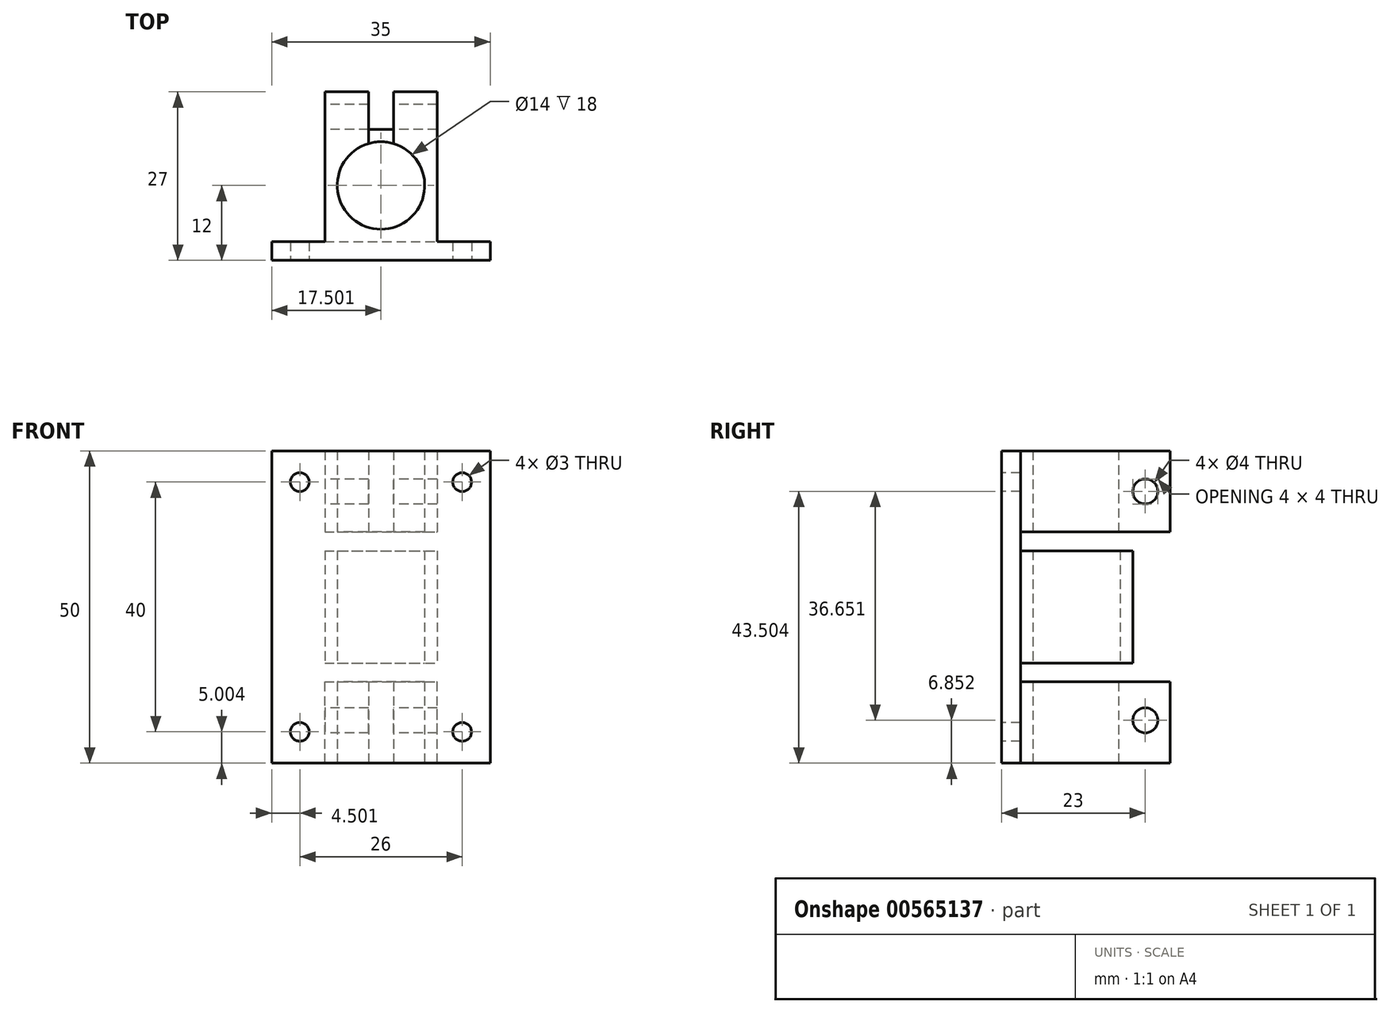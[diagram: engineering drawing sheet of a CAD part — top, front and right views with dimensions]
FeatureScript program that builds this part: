
annotation { "Feature Type Name" : "Feature", "Feature Type Description" : "" }
export const myFeature = defineFeature(function(context is Context, id is Id, definition is map)
    precondition{}
    {
        {
            var Q0;
            Q0=qCreatedBy(makeId("Front.planeOp"),FACE);
            var sketch = newSketch(context, id + "F0", { "sketchPlane" : qUnion([Q0])});
            skLineSegment(sketch, "E0.bottom", {"start": v(20, 24.93) * mm, "end": v(-15, 24.93) * mm});
            skLineSegment(sketch, "E0.top", {"start": v(20, -25.07) * mm, "end": v(-15, -25.07) * mm});
            skLineSegment(sketch, "E0.left", {"start": v(20, 24.93) * mm, "end": v(20, -25.07) * mm});
            skLineSegment(sketch, "E0.right", {"start": v(-15, 24.93) * mm, "end": v(-15, -25.07) * mm});
            skPoint(sketch, "E0.middle", {"position": v(2.5, -0.07) * mm});
            skSolve(sketch);
        }
        {
            var Q0;
            Q0=makeQuery(id+"F0.imprint","IMPRINT",FACE,{"disambiguationData":[TD([[makeQuery(id+"F0.imprint","IMPRINT",EDGE,{"derivedFrom":sQuery(id+"F0.wireOp",EDGE,"E0.bottom")}),1.0]])]});
            extrude(context, id + "F1", {"entities" : qUnion([Q0]), "oppositeDirection" : true, "depth" : 3 * mm, "offsetDistance" : 25 * mm});
        }
        {
            var Q0;
            Q0=makeQuery(id+"F1.opExtrude","CAP_FACE",FACE,{"disambiguationData":[OSD([sQuery(id+"F0.wireOp",EDGE,"E0.bottom"),sQuery(id+"F0.wireOp",EDGE,"E0.top"),sQuery(id+"F0.wireOp",EDGE,"E0.left"),sQuery(id+"F0.wireOp",EDGE,"E0.right")])],"isStart":false});
            var sketch = newSketch(context, id + "F2", { "sketchPlane" : qUnion([Q0])});
            skLineSegment(sketch, "E1.bottom", {"start": v(6.5, 24.93) * mm, "end": v(-11.5, 24.93) * mm});
            skLineSegment(sketch, "E1.top", {"start": v(6.5, 11.93) * mm, "end": v(-11.5, 11.93) * mm});
            skLineSegment(sketch, "E1.left", {"start": v(6.5, 24.93) * mm, "end": v(6.5, 11.93) * mm});
            skLineSegment(sketch, "E1.right", {"start": v(-11.5, 24.93) * mm, "end": v(-11.5, 11.93) * mm});
            skPoint(sketch, "E1.middle", {"position": v(-2.5, 18.43) * mm});
            skPoint(sketch, "E1.middle.positionSnap0", {"position": v(-2.5, 24.93) * mm});
            skPoint(sketch, "E1.centerSnap0", {"position": v(-2.5, 24.93) * mm});
            skLineSegment(sketch, "E2.bottom", {"start": v(6.5, 8.93) * mm, "end": v(-11.5, 8.93) * mm});
            skLineSegment(sketch, "E2.top", {"start": v(6.5, -9.07) * mm, "end": v(-11.5, -9.07) * mm});
            skLineSegment(sketch, "E2.left", {"start": v(6.5, 8.93) * mm, "end": v(6.5, -9.07) * mm});
            skLineSegment(sketch, "E2.right", {"start": v(-11.5, 8.93) * mm, "end": v(-11.5, -9.07) * mm});
            skPoint(sketch, "E2.middle", {"position": v(-2.5, -0.07) * mm});
            skLineSegment(sketch, "E3.bottom", {"start": v(6.5, -25.07) * mm, "end": v(-11.5, -25.07) * mm});
            skLineSegment(sketch, "E3.top", {"start": v(6.5, -12.07) * mm, "end": v(-11.5, -12.07) * mm});
            skLineSegment(sketch, "E3.left", {"start": v(6.5, -25.07) * mm, "end": v(6.5, -12.07) * mm});
            skLineSegment(sketch, "E3.right", {"start": v(-11.5, -25.07) * mm, "end": v(-11.5, -12.07) * mm});
            skPoint(sketch, "E3.middle", {"position": v(-2.5, -18.57) * mm});
            skSolve(sketch);
        }
        {
            var Q0;
            Q0=makeQuery(id+"F2.imprint","IMPRINT",FACE,{"disambiguationData":[TD([[makeQuery(id+"F2.imprint","IMPRINT",EDGE,{"derivedFrom":sQuery(id+"F2.wireOp",EDGE,"E1.bottom")}),-1.0]])]});
            var Q1;
            Q1=makeQuery(id+"F2.imprint","IMPRINT",FACE,{"disambiguationData":[TD([[makeQuery(id+"F2.imprint","IMPRINT",EDGE,{"derivedFrom":sQuery(id+"F2.wireOp",EDGE,"E2.bottom")}),1.0]])]});
            var Q2;
            Q2=makeQuery(id+"F2.imprint","IMPRINT",FACE,{"disambiguationData":[TD([[makeQuery(id+"F2.imprint","IMPRINT",EDGE,{"derivedFrom":sQuery(id+"F2.wireOp",EDGE,"E3.bottom")}),1.0]])]});
            extrude(context, id + "F3", {"entities" : qUnion([Q0, Q1, Q2]), "operationType" : NewBodyOperationType.ADD, "depth" : 24 * mm, "offsetDistance" : 25 * mm});
        }
        {
            var Q0;
            Q0=makeQuery(id+"F3.boolean.opBoolean","MERGE",FACE,{"derivedFrom":[makeQuery(id+"F1.opExtrude","SWEPT_FACE",FACE,{"disambiguationData":[OSD([sQuery(id+"F0.wireOp",EDGE,"E0.top")])]}),makeQuery(id+"F3.opExtrude","SWEPT_FACE",FACE,{"disambiguationData":[OSD([sQuery(id+"F2.wireOp",EDGE,"E3.bottom")])]})]});
            var sketch = newSketch(context, id + "F4", { "sketchPlane" : qUnion([Q0])});
            skCircle(sketch, "E4", {"center": v(2.5, -12) * mm, "radius": 7 * mm});
            skSolve(sketch);
        }
        {
            var Q0;
            Q0 = qSketchRegion(id + "F4", true);
            extrude(context, id + "F5", {"entities" : qUnion([Q0]), "operationType" : NewBodyOperationType.REMOVE, "oppositeDirection" : true, "depth" : 50 * mm, "offsetDistance" : 25 * mm});
        }
        {
            var Q0;
            Q0=makeQuery(id+"F3.opExtrude","SWEPT_FACE",FACE,{"disambiguationData":[OSD([sQuery(id+"F2.wireOp",EDGE,"E1.left")])]});
            var sketch = newSketch(context, id + "F6", { "sketchPlane" : qUnion([Q0])});
            skCircle(sketch, "E5", {"center": v(-23, 18.43) * mm, "radius": 2 * mm});
            skPoint(sketch, "E5.centerSnap0", {"position": v(-27, 18.43) * mm});
            skCircle(sketch, "E6", {"center": v(-23, -18.22) * mm, "radius": 2 * mm});
            skSolve(sketch);
        }
        {
            var Q0;
            Q0=makeQuery(id+"F6.imprint","IMPRINT",FACE,{"disambiguationData":[TD([[makeQuery(id+"F6.imprint","IMPRINT",EDGE,{"derivedFrom":sQuery(id+"F6.wireOp",EDGE,"E5")}),1.0]])]});
            var Q1;
            Q1=makeQuery(id+"F6.imprint","IMPRINT",FACE,{"disambiguationData":[TD([[makeQuery(id+"F6.imprint","IMPRINT",EDGE,{"derivedFrom":sQuery(id+"F6.wireOp",EDGE,"E6")}),1.0]])]});
            extrude(context, id + "F7", {"entities" : qUnion([Q0, Q1]), "operationType" : NewBodyOperationType.REMOVE, "oppositeDirection" : true, "depth" : 25 * mm, "offsetDistance" : 25 * mm});
        }
        {
            var Q0;
            Q0=makeQuery(id+"F3.opExtrude","CAP_FACE",FACE,{"disambiguationData":[OSD([sQuery(id+"F2.wireOp",EDGE,"E1.bottom"),sQuery(id+"F2.wireOp",EDGE,"E1.top"),sQuery(id+"F2.wireOp",EDGE,"E1.left"),sQuery(id+"F2.wireOp",EDGE,"E1.right")])],"isStart":false});
            var sketch = newSketch(context, id + "F8", { "sketchPlane" : qUnion([Q0])});
            skLineSegment(sketch, "E7", {"start": v(-2.5, 24.93) * mm, "end": v(-2.5, 11.93) * mm, "construction": true});
            skLineSegment(sketch, "E8", {"start": v(-2.5, 11.93) * mm, "end": v(-11.5, 18.43) * mm, "construction": true});
            skLineSegment(sketch, "E9", {"start": v(-11.5, 18.43) * mm, "end": v(6.5, 18.43) * mm, "construction": true});
            skLineSegment(sketch, "E10.bottom", {"start": v(-0.5, 24.93) * mm, "end": v(-4.5, 24.93) * mm});
            skLineSegment(sketch, "E10.top", {"start": v(-0.5, 11.93) * mm, "end": v(-4.5, 11.93) * mm});
            skLineSegment(sketch, "E10.left", {"start": v(-0.5, 24.93) * mm, "end": v(-0.5, 11.93) * mm});
            skLineSegment(sketch, "E10.right", {"start": v(-4.5, 24.93) * mm, "end": v(-4.5, 11.93) * mm});
            skPoint(sketch, "E10.middle", {"position": v(-2.5, 18.43) * mm});
            skSolve(sketch);
        }
        {
            var Q0;
            Q0=makeQuery(id+"F8.imprint","IMPRINT",FACE,{"disambiguationData":[TD([[makeQuery(id+"F8.imprint","IMPRINT",EDGE,{"derivedFrom":sQuery(id+"F8.wireOp",EDGE,"E10.bottom")}),-1.0]])]});
            extrude(context, id + "F9", {"entities" : qUnion([Q0]), "operationType" : NewBodyOperationType.REMOVE, "oppositeDirection" : true, "depth" : 10 * mm, "offsetDistance" : 25 * mm});
        }
        {
            var Q0;
            Q0=makeQuery(id+"F3.opExtrude","CAP_FACE",FACE,{"disambiguationData":[OSD([sQuery(id+"F2.wireOp",EDGE,"E3.bottom"),sQuery(id+"F2.wireOp",EDGE,"E3.top"),sQuery(id+"F2.wireOp",EDGE,"E3.left"),sQuery(id+"F2.wireOp",EDGE,"E3.right")])],"isStart":false});
            var sketch = newSketch(context, id + "F10", { "sketchPlane" : qUnion([Q0])});
            skLineSegment(sketch, "E11", {"start": v(-2.5, -12.07) * mm, "end": v(-2.5, -25.07) * mm, "construction": true});
            skLineSegment(sketch, "E12", {"start": v(-2.5, -25.07) * mm, "end": v(-11.5, -18.57) * mm, "construction": true});
            skLineSegment(sketch, "E13", {"start": v(-11.5, -18.57) * mm, "end": v(6.5, -18.57) * mm, "construction": true});
            skLineSegment(sketch, "E14.bottom", {"start": v(-0.5, -12.07) * mm, "end": v(-4.5, -12.07) * mm});
            skLineSegment(sketch, "E14.top", {"start": v(-0.5, -25.07) * mm, "end": v(-4.5, -25.07) * mm});
            skLineSegment(sketch, "E14.left", {"start": v(-0.5, -12.07) * mm, "end": v(-0.5, -25.07) * mm});
            skLineSegment(sketch, "E14.right", {"start": v(-4.5, -12.07) * mm, "end": v(-4.5, -25.07) * mm});
            skPoint(sketch, "E14.middle", {"position": v(-2.5, -18.57) * mm});
            skSolve(sketch);
        }
        {
            var Q0;
            Q0=makeQuery(id+"F10.imprint","IMPRINT",FACE,{"disambiguationData":[TD([[makeQuery(id+"F10.imprint","IMPRINT",EDGE,{"derivedFrom":sQuery(id+"F10.wireOp",EDGE,"E14.bottom")}),1.0]])]});
            extrude(context, id + "F11", {"entities" : qUnion([Q0]), "operationType" : NewBodyOperationType.REMOVE, "oppositeDirection" : true, "depth" : 10 * mm, "offsetDistance" : 25 * mm});
        }
        {
            var Q0;
            Q0=makeQuery(id+"F1.opExtrude","CAP_FACE",FACE,{"disambiguationData":[OSD([sQuery(id+"F0.wireOp",EDGE,"E0.bottom"),sQuery(id+"F0.wireOp",EDGE,"E0.top"),sQuery(id+"F0.wireOp",EDGE,"E0.left"),sQuery(id+"F0.wireOp",EDGE,"E0.right")])],"isStart":true});
            var sketch = newSketch(context, id + "F12", { "sketchPlane" : qUnion([Q0])});
            skCircle(sketch, "E15", {"center": v(-10.5, 19.93) * mm, "radius": 1.5 * mm});
            skCircle(sketch, "E16", {"center": v(15.5, 19.93) * mm, "radius": 1.5 * mm});
            skCircle(sketch, "E17", {"center": v(-10.5, -20.07) * mm, "radius": 1.5 * mm});
            skCircle(sketch, "E18", {"center": v(15.5, -20.07) * mm, "radius": 1.5 * mm});
            skSolve(sketch);
        }
        {
            var Q0;
            Q0=makeQuery(id+"F12.imprint","IMPRINT",FACE,{"disambiguationData":[TD([[makeQuery(id+"F12.imprint","IMPRINT",EDGE,{"derivedFrom":sQuery(id+"F12.wireOp",EDGE,"E16")}),1.0]])]});
            var Q1;
            Q1=makeQuery(id+"F12.imprint","IMPRINT",FACE,{"disambiguationData":[TD([[makeQuery(id+"F12.imprint","IMPRINT",EDGE,{"derivedFrom":sQuery(id+"F12.wireOp",EDGE,"E17")}),1.0]])]});
            var Q2;
            Q2=makeQuery(id+"F12.imprint","IMPRINT",FACE,{"disambiguationData":[TD([[makeQuery(id+"F12.imprint","IMPRINT",EDGE,{"derivedFrom":sQuery(id+"F12.wireOp",EDGE,"E18")}),1.0]])]});
            var Q3;
            Q3=makeQuery(id+"F12.imprint","IMPRINT",FACE,{"disambiguationData":[TD([[makeQuery(id+"F12.imprint","IMPRINT",EDGE,{"derivedFrom":sQuery(id+"F12.wireOp",EDGE,"E15")}),1.0]])]});
            extrude(context, id + "F13", {"entities" : qUnion([Q0, Q1, Q2, Q3]), "operationType" : NewBodyOperationType.REMOVE, "oppositeDirection" : true, "depth" : 5 * mm, "offsetDistance" : 25 * mm});
        }
        {
            var Q0;
            Q0=makeQuery(id+"F3.opExtrude","SWEPT_FACE",FACE,{"disambiguationData":[OSD([sQuery(id+"F2.wireOp",EDGE,"E2.left")])]});
            var sketch = newSketch(context, id + "F14", { "sketchPlane" : qUnion([Q0])});
            skLineSegment(sketch, "E19.bottom", {"start": v(-27, 8.93) * mm, "end": v(-21, 8.93) * mm});
            skLineSegment(sketch, "E19.top", {"start": v(-27, -9.07) * mm, "end": v(-21, -9.07) * mm});
            skLineSegment(sketch, "E19.left", {"start": v(-27, 8.93) * mm, "end": v(-27, -9.07) * mm});
            skLineSegment(sketch, "E19.right", {"start": v(-21, 8.93) * mm, "end": v(-21, -9.07) * mm});
            skSolve(sketch);
        }
        {
            var Q0;
            Q0=makeQuery(id+"F14.imprint","IMPRINT",FACE,{"disambiguationData":[TD([[makeQuery(id+"F14.imprint","IMPRINT",EDGE,{"derivedFrom":sQuery(id+"F14.wireOp",EDGE,"E19.bottom")}),-1.0]])]});
            extrude(context, id + "F15", {"entities" : qUnion([Q0]), "operationType" : NewBodyOperationType.REMOVE, "oppositeDirection" : true, "depth" : 18 * mm, "offsetDistance" : 25 * mm});
        }
    });
